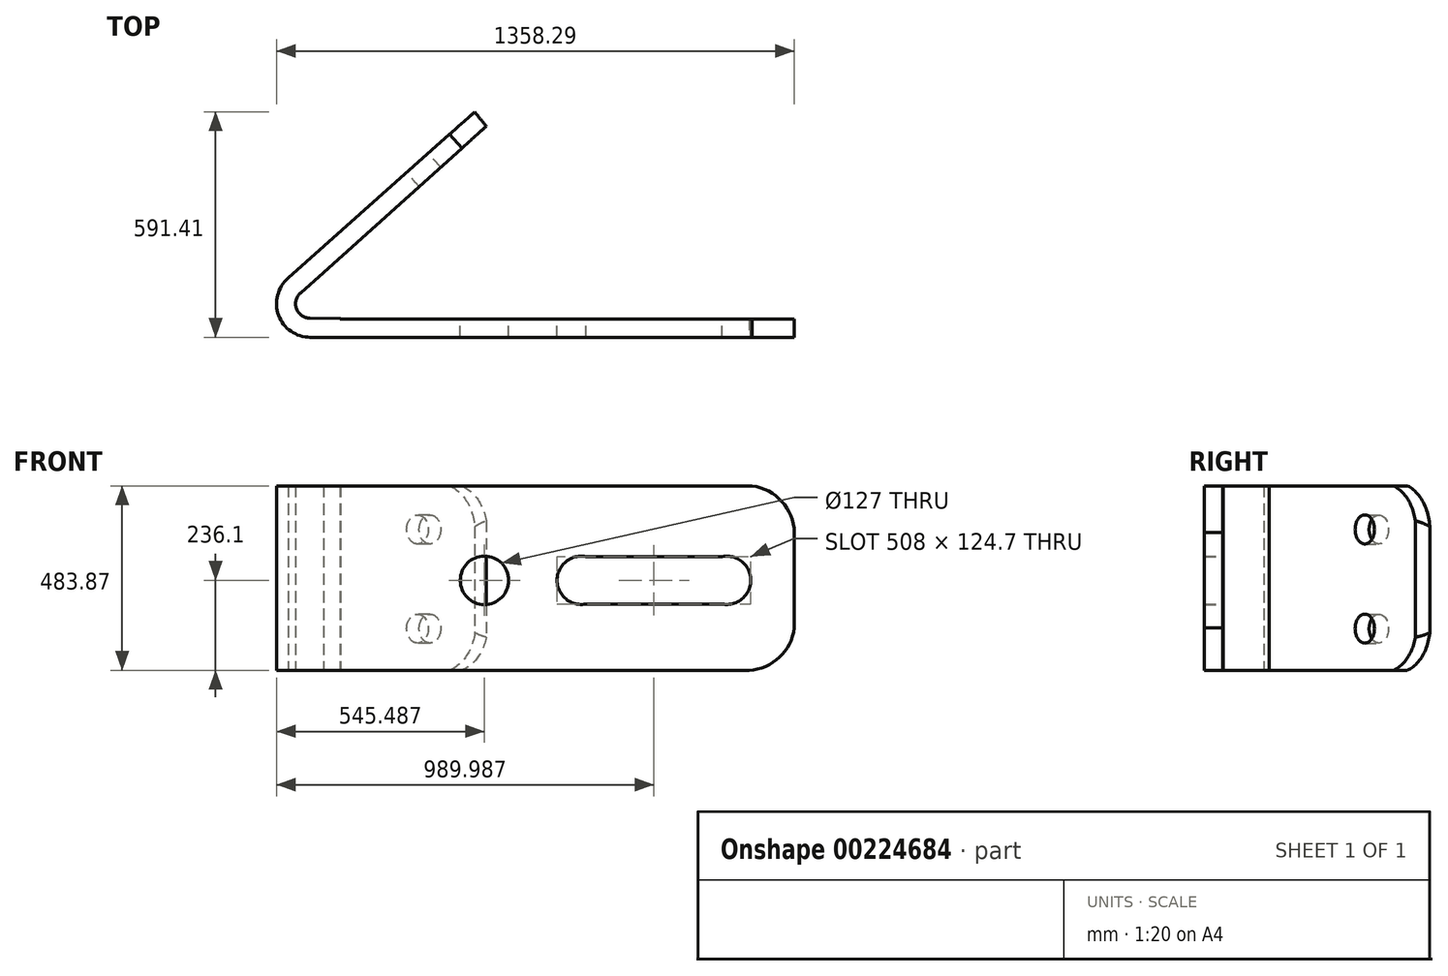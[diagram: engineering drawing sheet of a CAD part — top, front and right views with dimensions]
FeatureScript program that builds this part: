
annotation { "Feature Type Name" : "Feature", "Feature Type Description" : "" }
export const myFeature = defineFeature(function(context is Context, id is Id, definition is map)
    precondition{}
    {
        {
            var Q0;
            Q0=qCreatedBy(makeId("Top.planeOp"),FACE);
            var sketch = newSketch(context, id + "F0", { "sketchPlane" : qUnion([Q0])});
            skLineSegment(sketch, "E0.bottom", {"start": v(-634.86, -12.65) * mm, "end": v(635.14, -12.65) * mm});
            skLineSegment(sketch, "E0.top", {"start": v(-634.86, -60.91) * mm, "end": v(635.14, -60.91) * mm});
            skLineSegment(sketch, "E0.left", {"start": v(-634.86, -12.65) * mm, "end": v(-634.86, -60.91) * mm});
            skLineSegment(sketch, "E0.right", {"start": v(635.14, -12.65) * mm, "end": v(635.14, -60.91) * mm});
            skCircle(sketch, "E1", {"center": v(-634.86, 27.37) * mm, "radius": 38.1 * mm});
            skCircle(sketch, "E2", {"center": v(-634.86, 27.37) * mm, "radius": 88.28 * mm});
            skLineSegment(sketch, "E3", {"start": v(-653.6, 60.54) * mm, "end": v(-173.07, 492.67) * mm});
            skLineSegment(sketch, "E4", {"start": v(-203.03, 530.5) * mm, "end": v(-173.07, 492.67) * mm});
            skLineSegment(sketch, "E5", {"start": v(-675.2, 105.9) * mm, "end": v(-694.96, 92.04) * mm});
            skLineSegment(sketch, "E6", {"start": v(-694.96, 92.04) * mm, "end": v(-203.03, 530.5) * mm});
            skSolve(sketch);
        }
        {
            var Q0;
            Q0 = qSketchRegion(id + "F0", true);
            extrude(context, id + "F1", {"entities" : qUnion([Q0]), "depth" : 483.87 * mm});
        }
        {
            var Q0;
            Q0 = qSketchRegion(id + "F0", true);
            extrude(context, id + "F2", {"entities" : qUnion([Q0]), "operationType" : NewBodyOperationType.ADD, "depth" : 483.87 * mm});
        }
        {
            var Q0;
            Q0=makeQuery(id+"F1.opExtrude","SWEPT_FACE",FACE,{"disambiguationData":[OSD([sQuery(id+"F0.wireOp",EDGE,"E6")])]});
            var sketch = newSketch(context, id + "F3", { "sketchPlane" : qUnion([Q0])});
            skArc(sketch, "E7", {"start": v(-201.41, 98.05) * mm, "mid": v(-170.83, 36.57) * mm, "end": v(-112.72, 0) * mm});
            skArc(sketch, "E8", {"start": v(-112.72, 483.87) * mm, "mid": v(-173.06, 443.49) * mm, "end": v(-201.41, 376.64) * mm});
            skSolve(sketch);
        }
        {
            var Q0;
            Q0 = qSketchRegion(id + "F3", true);
            var Q1;
            {var subQ0=sQuery(id+"F3.wireOp",EDGE,"E7");Q1=makeQuery(id+"F3.imprint","IMPRINT",FACE,{"disambiguationData":[TD([[makeQuery(id+"F3.imprint","IMPRINT",EDGE,{"derivedFrom":subQ0}),-1.0]])]});}
            var Q2;
            {var subQ0=sQuery(id+"F3.wireOp",EDGE,"E8");Q2=makeQuery(id+"F3.imprint","IMPRINT",FACE,{"disambiguationData":[TD([[makeQuery(id+"F3.imprint","IMPRINT",EDGE,{"derivedFrom":subQ0}),-1.0]])]});}
            extrude(context, id + "F4", {"entities" : qUnion([Q0, Q1, Q2]), "operationType" : NewBodyOperationType.REMOVE, "oppositeDirection" : true, "depth" : 50.8 * mm});
        }
        {
            var Q0;
            Q0=makeQuery(id+"F1.opExtrude","SWEPT_FACE",FACE,{"disambiguationData":[OSD([sQuery(id+"F0.wireOp",EDGE,"E0.top")])]});
            var sketch = newSketch(context, id + "F5", { "sketchPlane" : qUnion([Q0])});
            skArc(sketch, "E9", {"start": v(635.14, 361.45) * mm, "mid": v(602.29, 443.17) * mm, "end": v(524.19, 483.87) * mm});
            skArc(sketch, "E10", {"start": v(516.56, 0) * mm, "mid": v(606.87, 45.66) * mm, "end": v(635.14, 142.82) * mm});
            skSolve(sketch);
        }
        {
            var Q0;
            Q0 = qSketchRegion(id + "F5", true);
            var Q1;
            {var subQ0=sQuery(id+"F5.wireOp",EDGE,"E10");var subQ1=sQuery(id+"F0.wireOp",EDGE,"E0.top");var subQ2=makeQuery(id+"F1.opExtrude","CAP_EDGE",EDGE,{"disambiguationData":[OSD([subQ1])],"isStart":true});var subQ3=makeQuery(id+"F5.imprint","INTERSECT",VERTEX,{"derivedFrom":[subQ2,subQ0]});Q1=makeQuery(id+"F5.imprint","IMPRINT",FACE,{"disambiguationData":[TD([[makeQuery(id+"F5.imprint","IMPRINT",EDGE,{"disambiguationData":[TD([[subQ3,-1.0]])],"derivedFrom":subQ0}),-1.0]])]});}
            var Q2;
            {var subQ0=sQuery(id+"F5.wireOp",EDGE,"E9");Q2=makeQuery(id+"F5.imprint","IMPRINT",FACE,{"disambiguationData":[TD([[makeQuery(id+"F5.imprint","IMPRINT",EDGE,{"derivedFrom":subQ0}),-1.0]])]});}
            extrude(context, id + "F6", {"entities" : qUnion([Q0, Q1, Q2]), "operationType" : NewBodyOperationType.REMOVE, "oppositeDirection" : true, "depth" : 50.8 * mm});
        }
        {
            var Q0;
            Q0=makeQuery(id+"F1.opExtrude","SWEPT_FACE",FACE,{"disambiguationData":[OSD([sQuery(id+"F0.wireOp",EDGE,"E6")])]});
            var sketch = newSketch(context, id + "F7", { "sketchPlane" : qUnion([Q0])});
            skCircle(sketch, "E11", {"center": v(0, 109.4) * mm, "radius": 38.1 * mm});
            skCircle(sketch, "E12", {"center": v(0, 369.57) * mm, "radius": 38.1 * mm});
            skSolve(sketch);
        }
        {
            var Q0;
            Q0=makeQuery(id+"F7.imprint","IMPRINT",FACE,{"disambiguationData":[TD([[makeQuery(id+"F7.imprint","IMPRINT",EDGE,{"derivedFrom":sQuery(id+"F7.wireOp",EDGE,"E12")}),1.0]])]});
            var Q1;
            Q1=makeQuery(id+"F7.imprint","IMPRINT",FACE,{"disambiguationData":[TD([[makeQuery(id+"F7.imprint","IMPRINT",EDGE,{"derivedFrom":sQuery(id+"F7.wireOp",EDGE,"E11")}),1.0]])]});
            extrude(context, id + "F8", {"entities" : qUnion([Q0, Q1]), "operationType" : NewBodyOperationType.REMOVE, "oppositeDirection" : true, "depth" : 50.8 * mm});
        }
        {
            var Q0;
            Q0=makeQuery(id+"F1.opExtrude","SWEPT_FACE",FACE,{"disambiguationData":[OSD([sQuery(id+"F0.wireOp",EDGE,"E0.bottom")])]});
            var sketch = newSketch(context, id + "F9", { "sketchPlane" : qUnion([Q0])});
            skCircle(sketch, "E13", {"center": v(177.66, 236.1) * mm, "radius": 63.5 * mm});
            skLineSegment(sketch, "E14.bottom", {"start": v(-76.34, 298.45) * mm, "end": v(-457.34, 298.45) * mm});
            skLineSegment(sketch, "E14.top", {"start": v(-76.34, 173.75) * mm, "end": v(-457.34, 173.75) * mm});
            skLineSegment(sketch, "E14.left", {"start": v(-457.34, 173.75) * mm, "end": v(-457.34, 298.45) * mm});
            skLineSegment(sketch, "E14.right", {"start": v(-76.34, 173.75) * mm, "end": v(-76.34, 298.45) * mm});
            skCircle(sketch, "E15", {"center": v(-76.34, 236.1) * mm, "radius": 63.5 * mm});
            skCircle(sketch, "E16", {"center": v(-457.34, 236.1) * mm, "radius": 63.5 * mm});
            skPoint(sketch, "E17.centerSnap0", {"position": v(-266.84, 298.45) * mm});
            skSolve(sketch);
        }
        {
            var Q0;
            {var subQ0=sQuery(id+"F9.wireOp",EDGE,"E14.right");Q0=makeQuery(id+"F9.imprint","IMPRINT",FACE,{"disambiguationData":[TD([[makeQuery(id+"F9.imprint","IMPRINT",EDGE,{"derivedFrom":subQ0}),1.0]])]});}
            var Q1;
            {var subQ0=sQuery(id+"F9.wireOp",EDGE,"E14.right");Q1=makeQuery(id+"F9.imprint","IMPRINT",FACE,{"disambiguationData":[TD([[makeQuery(id+"F9.imprint","IMPRINT",EDGE,{"derivedFrom":subQ0}),-1.0]])]});}
            var Q2;
            {var subQ0=sQuery(id+"F9.wireOp",EDGE,"E14.left");Q2=makeQuery(id+"F9.imprint","IMPRINT",FACE,{"disambiguationData":[TD([[makeQuery(id+"F9.imprint","IMPRINT",EDGE,{"derivedFrom":subQ0}),1.0]])]});}
            var Q3;
            {var subQ0=sQuery(id+"F9.wireOp",EDGE,"E14.left");Q3=makeQuery(id+"F9.imprint","IMPRINT",FACE,{"disambiguationData":[TD([[makeQuery(id+"F9.imprint","IMPRINT",EDGE,{"derivedFrom":subQ0}),-1.0]])]});}
            var Q4;
            {var subQ0=sQuery(id+"F9.wireOp",EDGE,"E15");var subQ1=sQuery(id+"F9.wireOp",EDGE,"E14.bottom");var subQ2=makeQuery(id+"F9.imprint","INTERSECT",VERTEX,{"derivedFrom":[subQ1,subQ0]});Q4=makeQuery(id+"F9.imprint","IMPRINT",FACE,{"disambiguationData":[TD([[makeQuery(id+"F9.imprint","IMPRINT",EDGE,{"disambiguationData":[TD([[subQ2,-1.0]])],"derivedFrom":subQ1}),1.0]])]});}
            var Q5;
            Q5=makeQuery(id+"F9.imprint","IMPRINT",FACE,{"disambiguationData":[TD([[makeQuery(id+"F9.imprint","IMPRINT",EDGE,{"derivedFrom":sQuery(id+"F9.wireOp",EDGE,"E13")}),1.0]])]});
            extrude(context, id + "F10", {"entities" : qUnion([Q0, Q1, Q2, Q3, Q4, Q5]), "operationType" : NewBodyOperationType.REMOVE, "oppositeDirection" : true, "depth" : 76.2 * mm});
        }
        {
            var Q0;
            Q0=makeQuery(id+"F1.opExtrude","CAP_FACE",FACE,{"disambiguationData":[OSD([sQuery(id+"F0.wireOp",EDGE,"E0.bottom"),sQuery(id+"F0.wireOp",EDGE,"E0.top"),sQuery(id+"F0.wireOp",EDGE,"E0.right"),sQuery(id+"F0.wireOp",EDGE,"E1"),sQuery(id+"F0.wireOp",EDGE,"E2"),sQuery(id+"F0.wireOp",EDGE,"E3"),sQuery(id+"F0.wireOp",EDGE,"E4"),sQuery(id+"F0.wireOp",EDGE,"E6")])],"isStart":false});
            var sketch = newSketch(context, id + "F11", { "sketchPlane" : qUnion([Q0])});
            skLineSegment(sketch, "E18", {"start": v(-600.2, 108.56) * mm, "end": v(-660.02, 55.99) * mm});
            skLineSegment(sketch, "E19", {"start": v(-600.2, 108.56) * mm, "end": v(-518.16, 89.63) * mm});
            skLineSegment(sketch, "E20", {"start": v(-518.16, 89.63) * mm, "end": v(-518.16, -12.65) * mm});
            skLineSegment(sketch, "E21", {"start": v(-518.16, -12.65) * mm, "end": v(-635.49, -10.73) * mm});
            skLineSegment(sketch, "E22", {"start": v(-635.49, -10.73) * mm, "end": v(-660.02, 55.99) * mm});
            skSolve(sketch);
        }
        {
            var Q0;
            Q0 = qSketchRegion(id + "F11", true);
            extrude(context, id + "F12", {"entities" : qUnion([Q0]), "operationType" : NewBodyOperationType.REMOVE, "oppositeDirection" : true, "depth" : 635 * mm});
        }
    });
